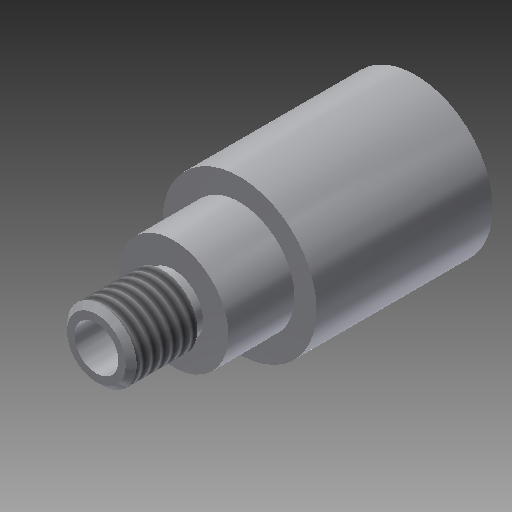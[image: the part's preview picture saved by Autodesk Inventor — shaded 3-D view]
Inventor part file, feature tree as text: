
AUTODESK INVENTOR PART (.ipt)
format: ipt  version: 2018 (Build 220112000, 112)  size: 174,080 bytes
history: native  units: mm
features: thread x2, revolve x1, chamfer x1
ambient origin geometry x8: Origin, YZ Plane, XZ Plane, XY Plane, X Axis, Y Axis, Z Axis, Center Point
bodies: Volumenkörper1 (feature_tree)
feature tree (4):
  revolve  "Umdrehung1"
  chamfer  "Fase1"  Distance=1.0mm
  thread  "Gewinde1"  [1 undecoded]
  thread  "Gewinde2"  [1 undecoded]
note: 2 required parameter values undecoded (feature->parameter linkage not recoverable at this tier; creation-order binding heuristic only, values carry confidence <= 0.55)
